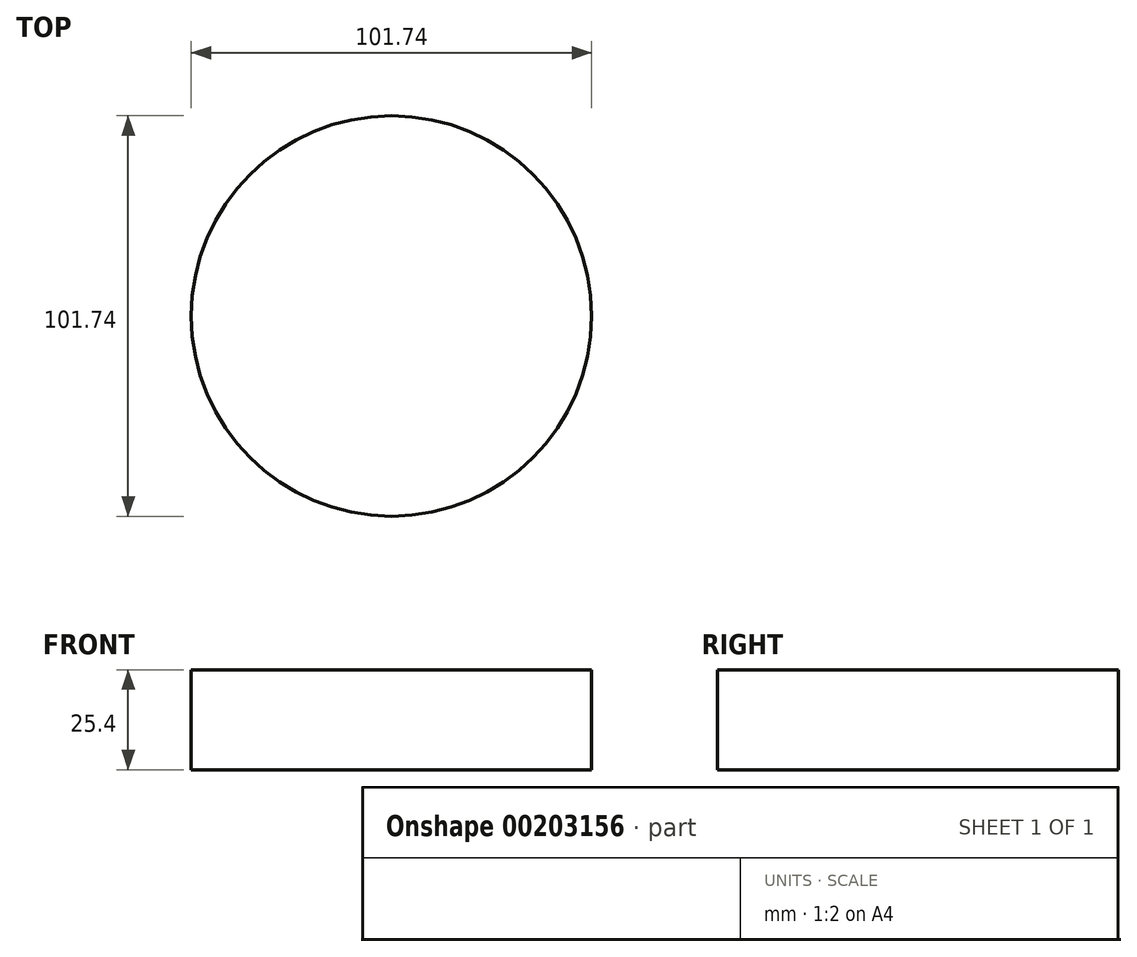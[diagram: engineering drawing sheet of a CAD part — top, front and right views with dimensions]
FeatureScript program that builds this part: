
annotation { "Feature Type Name" : "Feature", "Feature Type Description" : "" }
export const myFeature = defineFeature(function(context is Context, id is Id, definition is map)
    precondition{}
    {
        {
            var Q0;
            Q0=qCreatedBy(makeId("Top.planeOp"),FACE);
            var sketch = newSketch(context, id + "F0", { "sketchPlane" : qUnion([Q0])});
            skCircle(sketch, "E0", {"center": v(0, 0) * mm, "radius": 50.87 * mm});
            skSolve(sketch);
        }
        {
            var Q0;
            Q0 = qSketchRegion(id + "F0", true);
            extrude(context, id + "F1", {"entities" : qUnion([Q0]), "depth" : 25.4 * mm});
        }
    });
